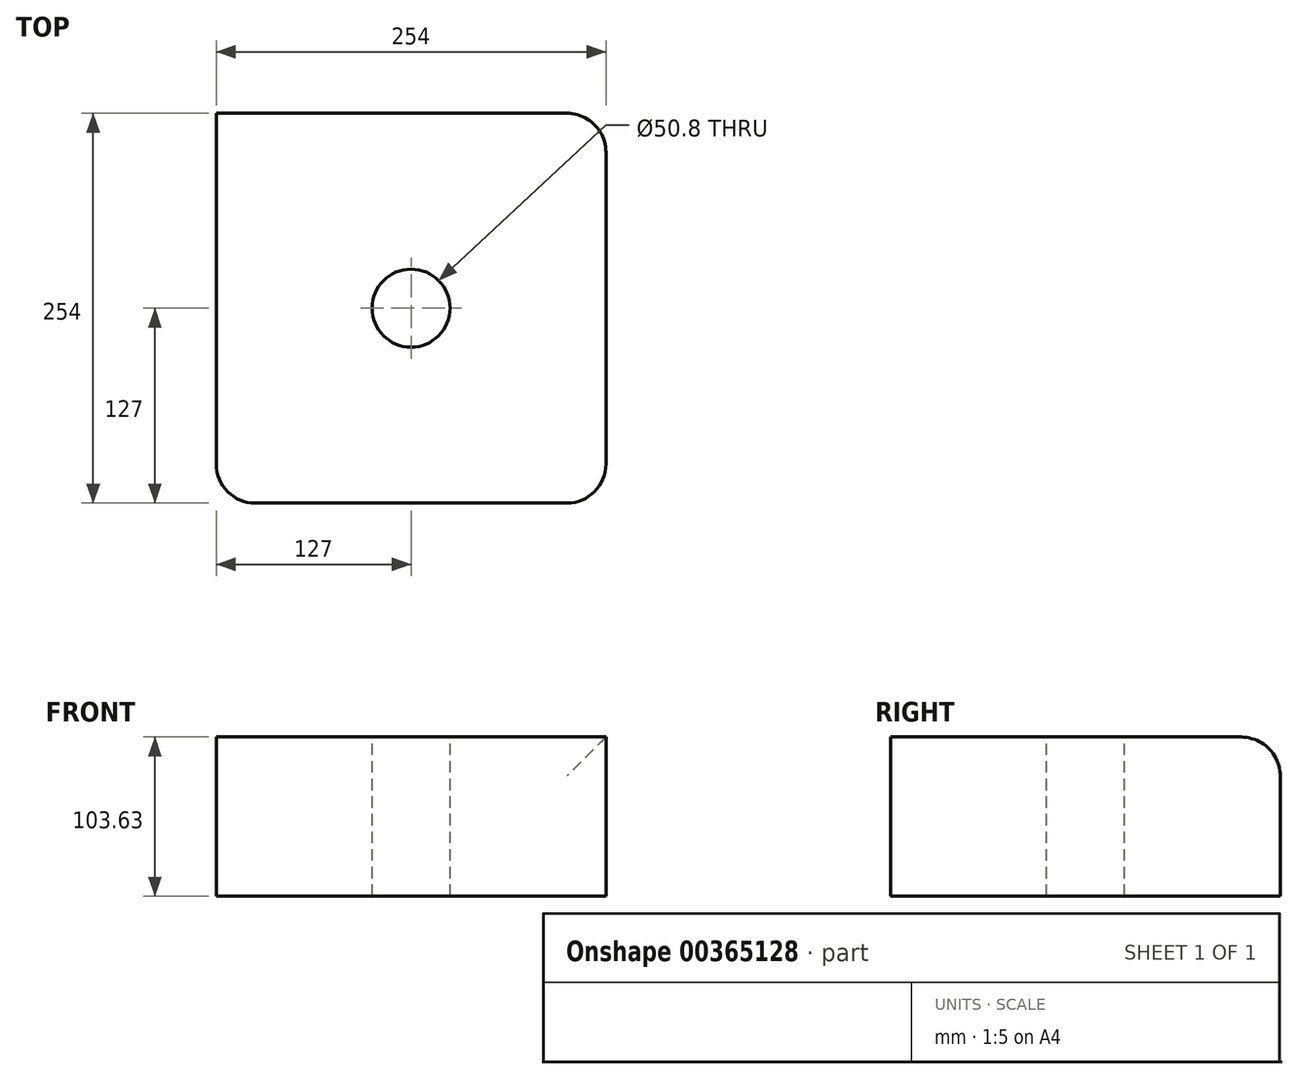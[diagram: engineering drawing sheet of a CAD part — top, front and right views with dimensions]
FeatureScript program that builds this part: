
annotation { "Feature Type Name" : "Feature", "Feature Type Description" : "" }
export const myFeature = defineFeature(function(context is Context, id is Id, definition is map)
    precondition{}
    {
        {
            var Q0;
            Q0=qCreatedBy(makeId("Top.planeOp"),FACE);
            var sketch = newSketch(context, id + "F0", { "sketchPlane" : qUnion([Q0])});
            skLineSegment(sketch, "E0.bottom", {"start": v(127, 127) * mm, "end": v(-127, 127) * mm});
            skLineSegment(sketch, "E0.top", {"start": v(127, -127) * mm, "end": v(-127, -127) * mm});
            skLineSegment(sketch, "E0.left", {"start": v(127, 127) * mm, "end": v(127, -127) * mm});
            skLineSegment(sketch, "E0.right", {"start": v(-127, 127) * mm, "end": v(-127, -127) * mm});
            skPoint(sketch, "E0.middle", {"position": v(0, 0) * mm});
            skSolve(sketch);
        }
        {
            var Q0;
            Q0=makeQuery(id+"F0.imprint","IMPRINT",FACE,{"disambiguationData":[TD([[makeQuery(id+"F0.imprint","IMPRINT",EDGE,{"derivedFrom":sQuery(id+"F0.wireOp",EDGE,"E0.bottom")}),1.0]])]});
            extrude(context, id + "F1", {"entities" : qUnion([Q0]), "oppositeDirection" : true, "depth" : 103.63 * mm});
        }
        {
            var Q0;
            Q0=makeQuery(id+"F1.opExtrude","SWEPT_EDGE",EDGE,{"disambiguationData":[OSD([sQuery(id+"F0.wireOp",EDGE,"E0.top"),sQuery(id+"F0.wireOp",EDGE,"E0.right")])]});
            var Q1;
            Q1=makeQuery(id+"F1.opExtrude","CAP_EDGE",EDGE,{"disambiguationData":[OSD([sQuery(id+"F0.wireOp",EDGE,"E0.bottom")])],"isStart":true});
            var Q2;
            Q2=makeQuery(id+"F1.opExtrude","SWEPT_EDGE",EDGE,{"disambiguationData":[OSD([sQuery(id+"F0.wireOp",EDGE,"E0.bottom"),sQuery(id+"F0.wireOp",EDGE,"E0.left")])]});
            var Q3;
            Q3=makeQuery(id+"F1.opExtrude","SWEPT_EDGE",EDGE,{"disambiguationData":[OSD([sQuery(id+"F0.wireOp",EDGE,"E0.top"),sQuery(id+"F0.wireOp",EDGE,"E0.left")])]});
            fillet(context, id + "F2", {"entities" : qUnion([Q0, Q1, Q2, Q3]), "radius" : 25.4 * mm, "tangentPropagation" : true, "allowEdgeOverflow" : false});
        }
        {
            var Q0;
            Q0=makeQuery(id+"F1.opExtrude","CAP_FACE",FACE,{"disambiguationData":[OSD([sQuery(id+"F0.wireOp",EDGE,"E0.bottom"),sQuery(id+"F0.wireOp",EDGE,"E0.top"),sQuery(id+"F0.wireOp",EDGE,"E0.left"),sQuery(id+"F0.wireOp",EDGE,"E0.right")])],"isStart":true});
            var sketch = newSketch(context, id + "F3", { "sketchPlane" : qUnion([Q0])});
            skCircle(sketch, "E1", {"center": v(0, 0) * mm, "radius": 38.1 * mm});
            skSolve(sketch);
        }
        {
            var Q0;
            Q0=sQuery(id+"F3.wireOp",VERTEX,"E1.center");
            var Q1;
            Q1=makeQuery(id+"F1.opExtrude","SWEPT_BODY",BODY,{"disambiguationData":[OSD([sQuery(id+"F0.wireOp",EDGE,"E0.bottom"),sQuery(id+"F0.wireOp",EDGE,"E0.top"),sQuery(id+"F0.wireOp",EDGE,"E0.left"),sQuery(id+"F0.wireOp",EDGE,"E0.right")])]});
            hole(context, id + "F4", {"style" : HoleStyle.SIMPLE, "endStyle" : HoleEndStyle.THROUGH, "holeDiameter" : 50.8 * mm, "isTappedThrough" : true, "tappedDepth" : 12.7 * mm, "tapClearance" : 3, "locations" : qUnion([Q0]), "scope" : qUnion([Q1])});
        }
    });
